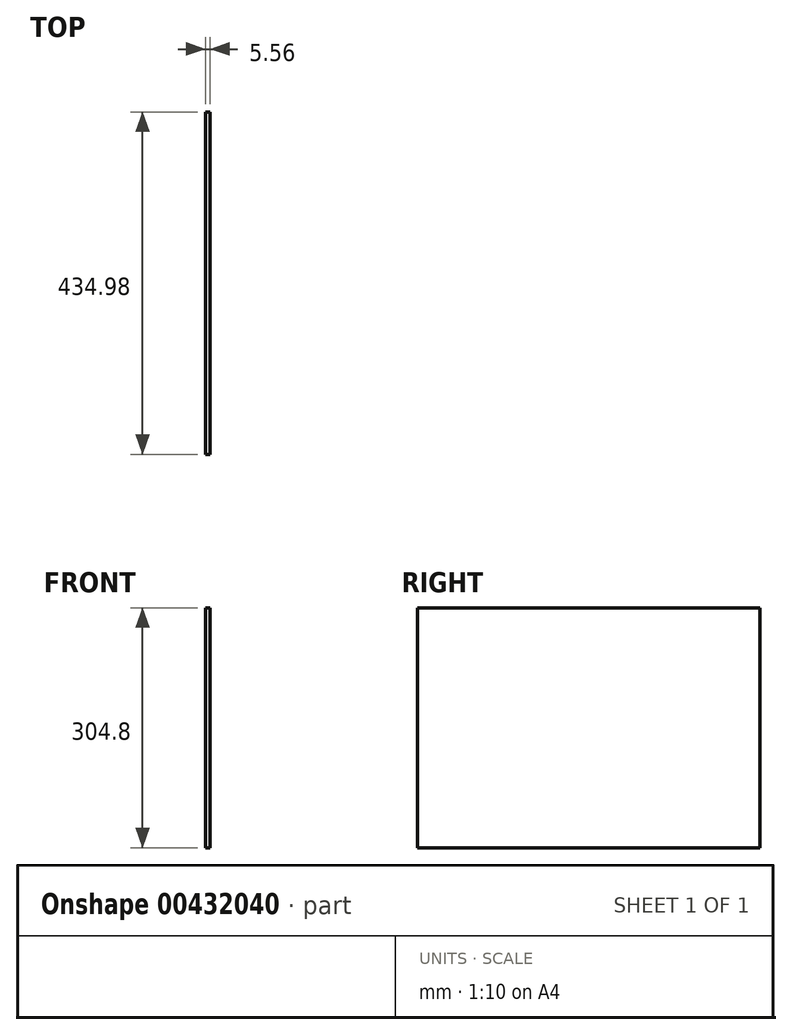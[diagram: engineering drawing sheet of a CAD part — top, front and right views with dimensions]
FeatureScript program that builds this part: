
annotation { "Feature Type Name" : "Feature", "Feature Type Description" : "" }
export const myFeature = defineFeature(function(context is Context, id is Id, definition is map)
    precondition{}
    {
        {
            var Q0;
            Q0=qCreatedBy(makeId("Right.planeOp"),FACE);
            var sketch = newSketch(context, id + "F0", { "sketchPlane" : qUnion([Q0])});
            skLineSegment(sketch, "E0", {"start": v(0, 0) * mm, "end": v(0, 6.35) * mm, "construction": true});
            skLineSegment(sketch, "E1", {"start": v(0, 6.35) * mm, "end": v(0, 158.75) * mm, "construction": true});
            skLineSegment(sketch, "E2.bottom", {"start": v(-217.49, 6.35) * mm, "end": v(217.49, 6.35) * mm});
            skLineSegment(sketch, "E2.top", {"start": v(-217.49, 311.15) * mm, "end": v(217.49, 311.15) * mm});
            skLineSegment(sketch, "E2.left", {"start": v(-217.49, 6.35) * mm, "end": v(-217.49, 311.15) * mm});
            skLineSegment(sketch, "E2.right", {"start": v(217.49, 6.35) * mm, "end": v(217.49, 311.15) * mm});
            skPoint(sketch, "E2.middle", {"position": v(0, 158.75) * mm});
            skSolve(sketch);
        }
        {
            var Q0;
            Q0 = qSketchRegion(id + "F0", true);
            extrude(context, id + "F1", {"entities" : qUnion([Q0]), "depth" : 5.56 * mm});
        }
    });
